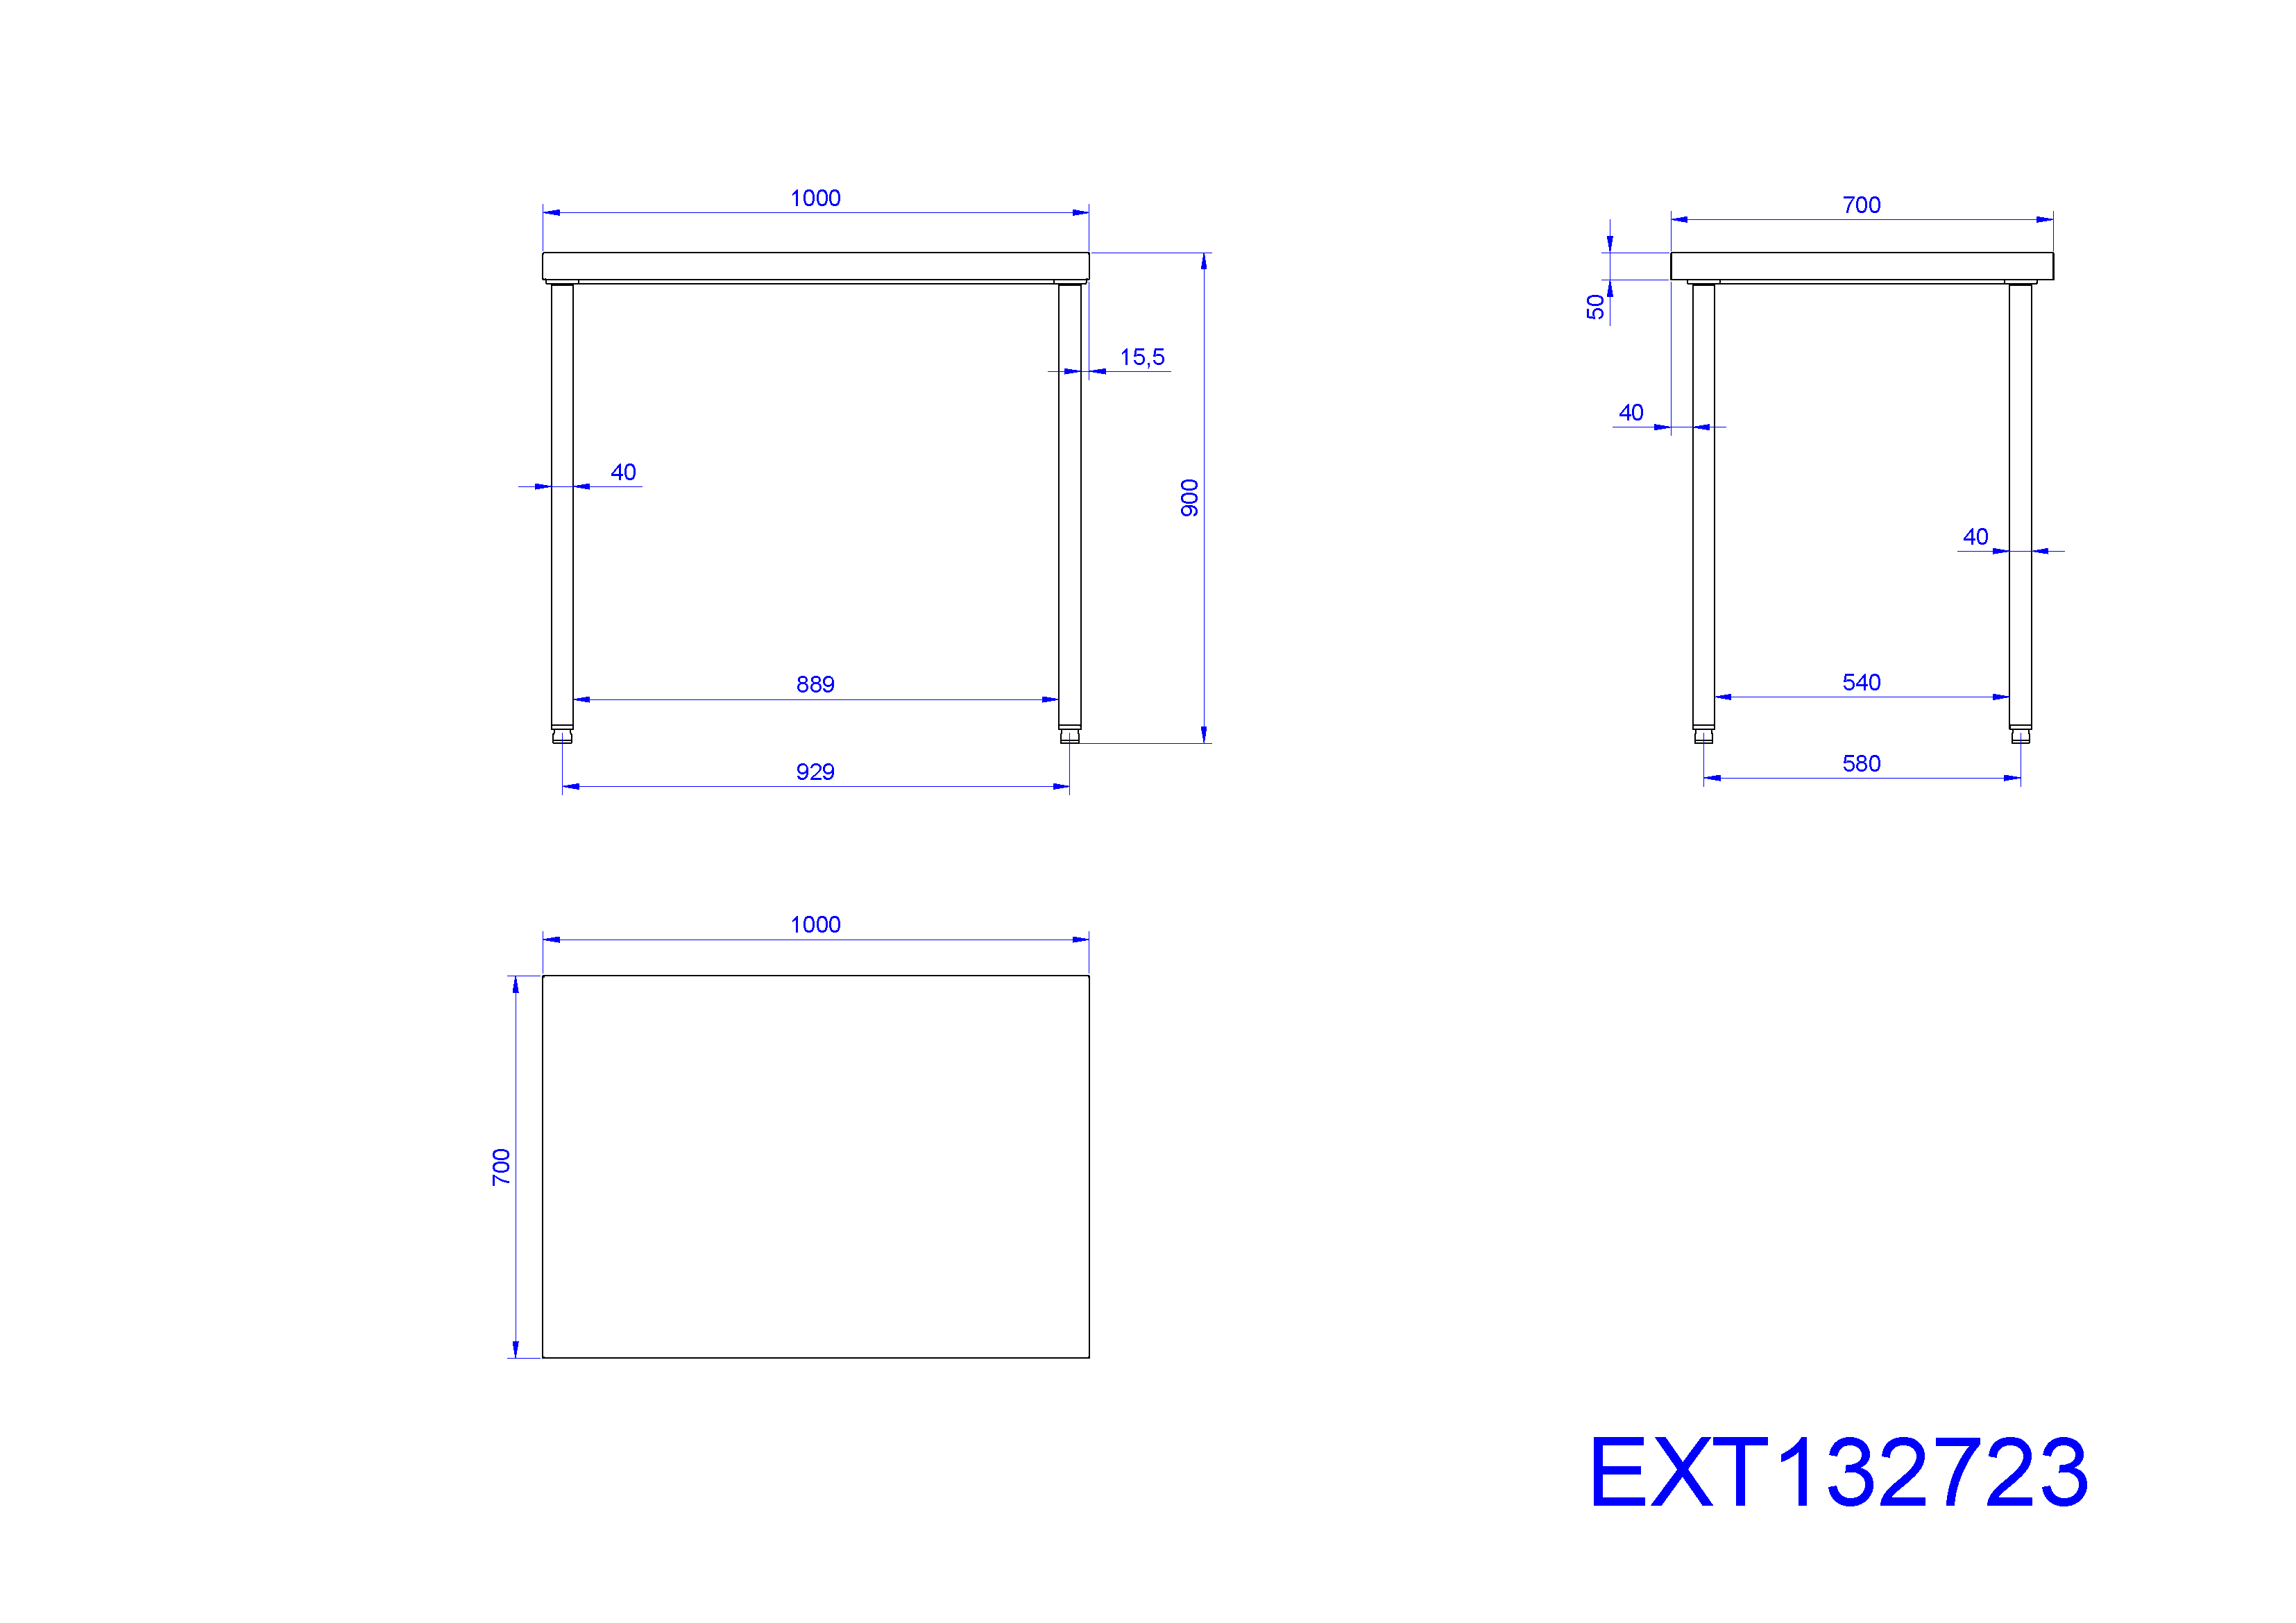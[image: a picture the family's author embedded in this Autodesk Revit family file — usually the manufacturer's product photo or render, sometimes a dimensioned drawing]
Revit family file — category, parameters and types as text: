
# Revit family: QF_ELECTROLUXPROFESSIONAL_133052_TG1800EN
name_source: partatom
category: Attrezzature speciali
units: mm (PartAtom-declared; Revit-internal decimal feet)

## family parameters
Basato su piano di lavoro = No
Condiviso = No
Punto di calcolo locali = No
Quota connettore circolare = Usa diametro
Sempre verticale = Sì
Taglio con vuoti quando caricato = No
Tipo di parte = Normale

## types (1)
- Standard
    Accessory = Sì
    Cold Water Size = 0 mm
    Compressed Air Pressure = 0.0 Pa
    Compressed Air Size = 0 mm
    Compressed Air Volume = 0.0 L/s
    Condensate Return Size = 0 mm
    Cycle = 0 Hz
    Depth Actual = 700 mm  [stored 2.29659 ft]
    Descrizione = WORK TABLE 1800 MM
    Direct Waste Size = 0 mm
    Gas Input Pressure = 0
    Gas KW = 0
    Gas Size = 0 mm
    HP = 0 HP
    Height Actual = 900 mm  [stored 2.95276 ft]
    Hot Water Size = 0 mm
    Item Number = 133052
    Length Actual = 1800 mm  [stored 5.90551 ft]
    Modello = TG1800EN
    Phase = 0
    Produttore = Electrolux Professional
    Prospetto di default = 0 mm  [stored 0 ft]
    Refrigerant Compressor Remote = Sì
    Refrigeration Liquid Line Size = 0 mm  [stored 0 ft]
    Refrigeration Suction Line Size = 0 mm  [stored 0 ft]
    Steam Consumption per Hour = 0
    Steam Supply Maximum Pressure = 0.0 Pa
    Steam Supply Minimum Pressure = 0.0 Pa
    Steam Supply Size = 0 mm
    URL = https://www.electroluxprofessional.com
    URL Manufacturer = https://www.electroluxprofessional.com
    Volts = 0 V
    Watts = 0 W
    Weight = 54.00 kg

note: source unit labels omitted for Gas Input Pressure — the stored unit's dimension contradicts the parameter name (converter mislabeling)

note: [stored X ft] marks values corroborated as IEEE doubles in the binary element streams (Revit-internal decimal feet)

## geometry (parser evidence)
native form markers: Sweep x2
no freeform markers — native parametric forms only
